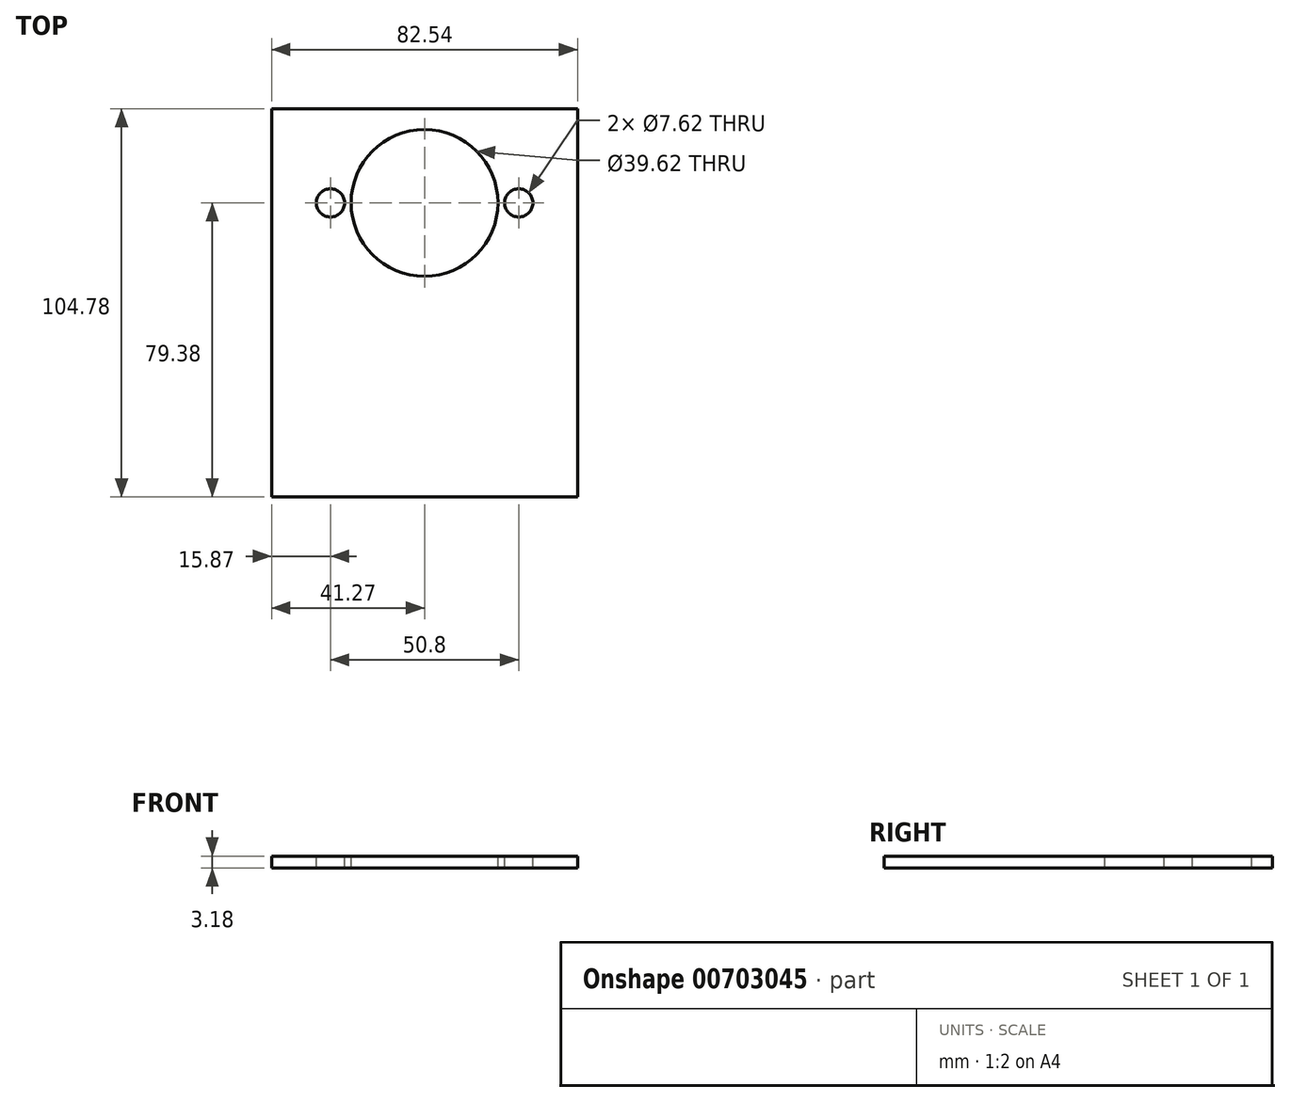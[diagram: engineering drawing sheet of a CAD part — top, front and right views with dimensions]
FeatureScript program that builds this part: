
annotation { "Feature Type Name" : "Feature", "Feature Type Description" : "" }
export const myFeature = defineFeature(function(context is Context, id is Id, definition is map)
    precondition{}
    {
        {
            var Q0;
            Q0=qCreatedBy(makeId("Top.planeOp"),FACE);
            var sketch = newSketch(context, id + "F0", { "sketchPlane" : qUnion([Q0])});
            skLineSegment(sketch, "E0.bottom", {"start": v(-41.28, 25.4) * mm, "end": v(41.28, 25.4) * mm});
            skLineSegment(sketch, "E0.top", {"start": v(-41.27, -79.37) * mm, "end": v(41.28, -79.37) * mm});
            skLineSegment(sketch, "E0.left", {"start": v(-41.28, 25.4) * mm, "end": v(-41.27, -79.38) * mm});
            skLineSegment(sketch, "E0.right", {"start": v(41.28, 25.4) * mm, "end": v(41.28, -79.38) * mm});
            skSolve(sketch);
        }
        {
            var Q0;
            Q0 = qSketchRegion(id + "FR5LTdiXmvA82zs_1", true);
            var Q1;
            Q1 = qSketchRegion(id + "F0", true);
            extrude(context, id + "F1", {"entities" : qUnion([Q0, Q1]), "depth" : 3.17 * mm, "offsetDistance" : 25.4 * mm});
        }
        {
            var Q0;
            Q0=makeQuery(id+"F1.opExtrude","CAP_FACE",FACE,{"disambiguationData":[OSD([sQuery(id+"F0.wireOp",EDGE,"E0.bottom"),sQuery(id+"F0.wireOp",EDGE,"E0.top"),sQuery(id+"F0.wireOp",EDGE,"E0.left"),sQuery(id+"F0.wireOp",EDGE,"E0.right")])],"isStart":false});
            var sketch = newSketch(context, id + "F2", { "sketchPlane" : qUnion([Q0])});
            skCircle(sketch, "E1", {"center": v(0, 0) * mm, "radius": 19.81 * mm});
            skCircle(sketch, "E2", {"center": v(-25.4, 0) * mm, "radius": 3.81 * mm});
            skCircle(sketch, "E3", {"center": v(25.4, 0) * mm, "radius": 3.81 * mm});
            skSolve(sketch);
        }
        {
            var Q0;
            Q0=makeQuery(id+"F2.imprint","IMPRINT",FACE,{"disambiguationData":[TD([[makeQuery(id+"F2.imprint","IMPRINT",EDGE,{"derivedFrom":sQuery(id+"F2.wireOp",EDGE,"E1")}),1.0]])]});
            var Q1;
            Q1=makeQuery(id+"F2.imprint","IMPRINT",FACE,{"disambiguationData":[TD([[makeQuery(id+"F2.imprint","IMPRINT",EDGE,{"derivedFrom":sQuery(id+"F2.wireOp",EDGE,"E2")}),1.0]])]});
            var Q2;
            Q2=makeQuery(id+"F2.imprint","IMPRINT",FACE,{"disambiguationData":[TD([[makeQuery(id+"F2.imprint","IMPRINT",EDGE,{"derivedFrom":sQuery(id+"F2.wireOp",EDGE,"E3")}),1.0]])]});
            var Q3;
            Q3=sQuery(id+"F2.wireOp",EDGE,"E1");
            extrude(context, id + "F3", {"entities" : qUnion([Q0, Q1, Q2]), "operationType" : NewBodyOperationType.REMOVE, "surfaceEntities" : qUnion([Q3]), "oppositeDirection" : true, "depth" : 25.4 * mm, "offsetDistance" : 25.4 * mm});
        }
    });
